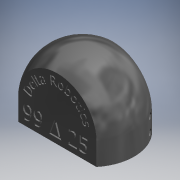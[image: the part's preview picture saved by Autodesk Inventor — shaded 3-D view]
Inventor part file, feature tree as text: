
AUTODESK INVENTOR PART (.ipt)
format: ipt  version: 2019 (Build 230136000, 136)  size: 732,160 bytes
history: native  units: mm (DEFAULTED — no unit token found)
features: sketch x11, extrude x10, plane x5, mirror x3, revolve x1
ambient origin geometry x8: Origin, YZ Plane, XZ Plane, XY Plane, X Axis, Y Axis, Z Axis, Center Point
bodies: Solid1 (feature_tree)
feature tree (30):
  extrude  "Extrusion1"  Depth=88.9mm
  extrude  "Extrusion2"  Depth=25.4mm
  extrude  "Extrusion3"  Depth=3.175mm TaperAngle=0.0deg
  plane  "Work Plane1"
  mirror  "Mirror1"
  plane  "Work Plane2"
  revolve  "Revolution1"  [1 undecoded]
  extrude  "Extrusion4"  Depth=44.45mm
  plane  "Work Plane3"
  mirror  "Mirror2"
  sketch  "Sketch7"  dims[d13=44.45mm d14=180.0deg]
  extrude  "Extrusion5"  TaperAngle=180.0deg  [1 undecoded]
  extrude  "Extrusion6"  Depth=6.35mm
  plane  "Work Plane4"
  extrude  "Extrusion7"  Depth=6.35mm
  plane  "Work Plane5"
  mirror  "Mirror3"
  extrude  "Extrusion8"  Depth=6.35mm
  extrude  "Extrusion9"  Depth=3.048mm
  extrude  "Extrusion10"  Depth=6.35mm TaperAngle=0.0deg
  sketch  "Sketch1"  dims[d0=82.55mm d1=88.9mm]
  sketch  "Sketch2"  dims[d2=25.4mm d3=25.4mm]
  sketch  "Sketch3"  dims[d4=59.69mm d5=0.0mm d6=3.175mm d7=0.0mm]
  sketch  "Sketch5"  dims[d8=12.7mm d9=25.4mm]
  sketch  "Sketch6"  dims[d10=9.525mm d11=0.0mm d12=44.45mm]
  sketch  "Sketch8"  dims[d15=25.4mm d16=0.0mm d18=6.35mm]
  sketch  "Sketch9"  dims[d19=6.35mm d20=8.001mm]
  sketch  "Sketch10"  dims[d21=24.003mm d22=6.35mm]
  sketch  "Sketch11"  dims[d23=2.54mm d24=0.0mm d25=3.048mm]
  sketch  "Sketch12"  dims[d26=3.048mm d27=2.54mm d28=0.0mm d29=6.35mm d30=6.35mm d31=19.05mm d32=0.0mm d33=38.1mm d34=1.27mm d35=0.0mm d36=1.5875mm d37=0.0mm d38=3.175mm d39=3.175mm d40=3.175mm d41=19.05mm d42=12.7mm d43=12.7mm d44=12.7mm d45=25.4mm d46=0.0mm]
note: 2 required parameter values undecoded (feature->parameter linkage not recoverable at this tier; creation-order binding heuristic only, values carry confidence <= 0.55)